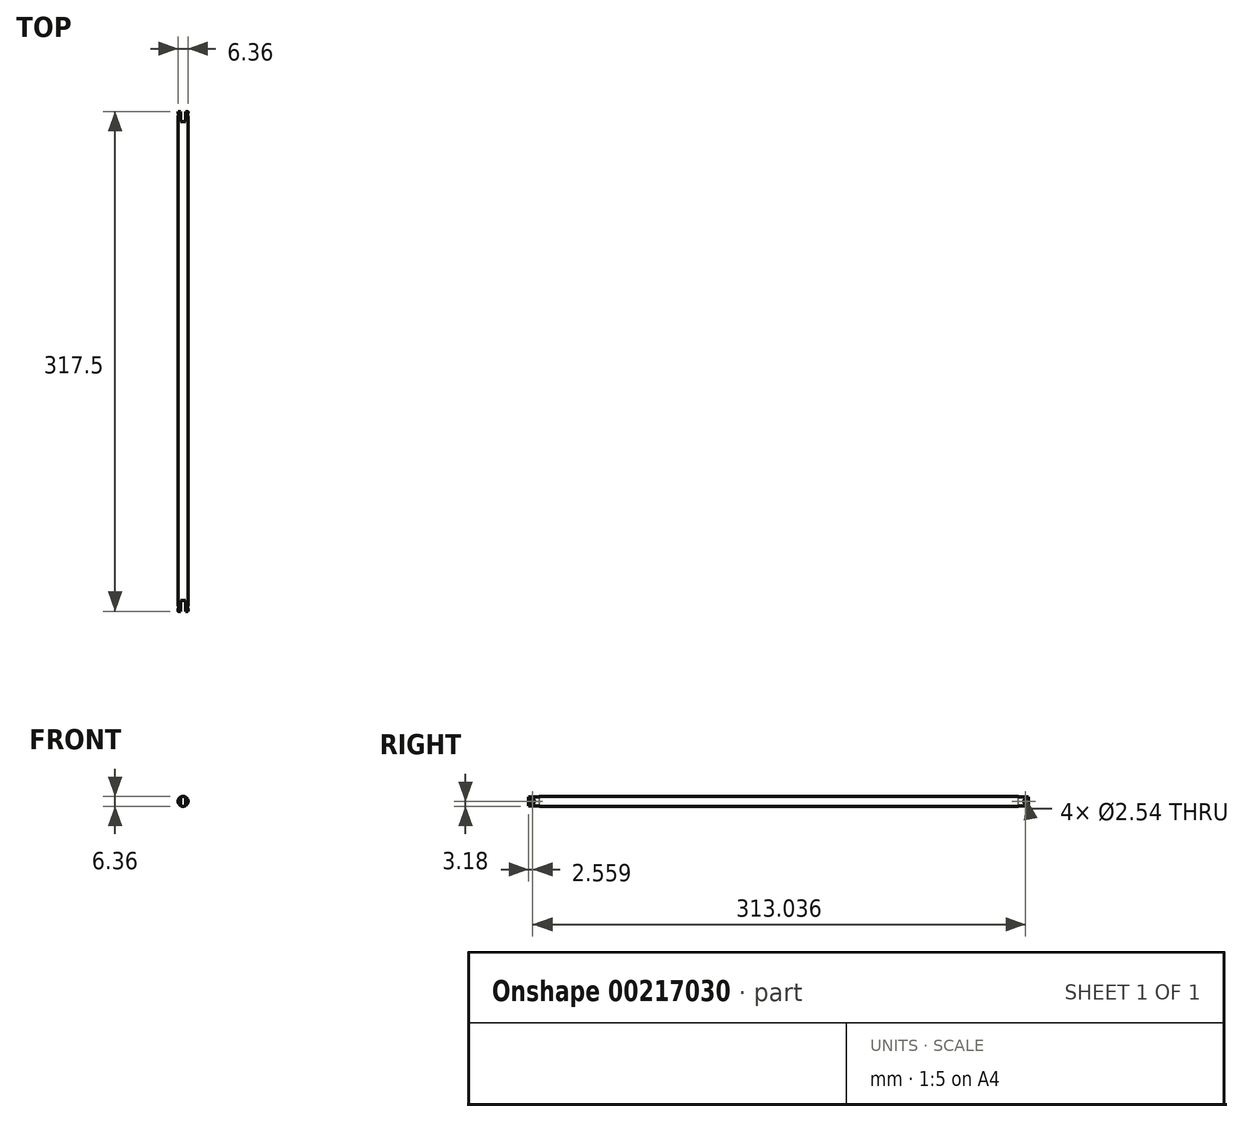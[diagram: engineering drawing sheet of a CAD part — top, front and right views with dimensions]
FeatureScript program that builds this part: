
annotation { "Feature Type Name" : "Feature", "Feature Type Description" : "" }
export const myFeature = defineFeature(function(context is Context, id is Id, definition is map)
    precondition{}
    {
        {
            var Q0;
            Q0=qCreatedBy(makeId("Front.planeOp"),FACE);
            var sketch = newSketch(context, id + "F0", { "sketchPlane" : qUnion([Q0])});
            skCircle(sketch, "E0", {"center": v(0, 0) * mm, "radius": 3.18 * mm});
            skSolve(sketch);
        }
        {
            var Q0;
            Q0=makeQuery(id+"F0.imprint","IMPRINT",FACE,{"disambiguationData":[TD([[makeQuery(id+"F0.imprint","IMPRINT",EDGE,{"derivedFrom":sQuery(id+"F0.wireOp",EDGE,"E0")}),1.0]])]});
            extrude(context, id + "F1", {"entities" : qUnion([Q0]), "depth" : 298.45 * mm});
        }
        {
            var Q0;
            Q0=qCreatedBy(makeId("Top.planeOp"),FACE);
            var sketch = newSketch(context, id + "F2", { "sketchPlane" : qUnion([Q0])});
            skLineSegment(sketch, "E1.bottom", {"start": v(1.59, -6.54) * mm, "end": v(-1.59, -6.54) * mm});
            skLineSegment(sketch, "E1.top", {"start": v(1.59, 6.54) * mm, "end": v(-1.59, 6.54) * mm});
            skLineSegment(sketch, "E1.left", {"start": v(1.59, -6.54) * mm, "end": v(1.59, 6.54) * mm});
            skLineSegment(sketch, "E1.right", {"start": v(-1.59, -6.54) * mm, "end": v(-1.59, 6.54) * mm});
            skPoint(sketch, "E1.middle", {"position": v(0, 0) * mm});
            skSolve(sketch);
        }
        {
            var Q0;
            Q0 = qSketchRegion(id + "F2", true);
            extrude(context, id + "F3", {"entities" : qUnion([Q0]), "operationType" : NewBodyOperationType.REMOVE, "oppositeDirection" : true, "depth" : 25.4 * mm, "symmetric" : true});
        }
        {
            var Q0;
            Q0=qCreatedBy(makeId("Right.planeOp"),FACE);
            var sketch = newSketch(context, id + "F4", { "sketchPlane" : qUnion([Q0])});
            skLineSegment(sketch, "E2", {"start": v(0, 0) * mm, "end": v(-1.9, 0) * mm, "construction": true});
            skCircle(sketch, "E3", {"center": v(-1.9, 0) * mm, "radius": 1.27 * mm});
            skSolve(sketch);
        }
        {
            var Q0;
            Q0 = qSketchRegion(id + "F4", true);
            extrude(context, id + "F5", {"entities" : qUnion([Q0]), "operationType" : NewBodyOperationType.REMOVE, "oppositeDirection" : true, "depth" : 25.4 * mm, "symmetric" : true});
        }
        {
            var Q0;
            Q0=makeQuery(id+"F1.opExtrude","CAP_FACE",FACE,{"disambiguationData":[OSD([sQuery(id+"F0.wireOp",EDGE,"E0")])],"isStart":false});
            extrude(context, id + "F6", {"entities" : qUnion([Q0]), "operationType" : NewBodyOperationType.ADD, "depth" : 19.05 * mm});
        }
        {
            var Q0;
            Q0=qCreatedBy(makeId("Top.planeOp"),FACE);
            var sketch = newSketch(context, id + "F7", { "sketchPlane" : qUnion([Q0])});
            skLineSegment(sketch, "E4.bottom", {"start": v(1.59, -323.33) * mm, "end": v(-1.59, -323.33) * mm});
            skLineSegment(sketch, "E4.top", {"start": v(1.59, -310.63) * mm, "end": v(-1.59, -310.63) * mm});
            skLineSegment(sketch, "E4.left", {"start": v(1.59, -323.33) * mm, "end": v(1.59, -310.63) * mm});
            skLineSegment(sketch, "E4.right", {"start": v(-1.59, -323.33) * mm, "end": v(-1.59, -310.63) * mm});
            skPoint(sketch, "E4.middle", {"position": v(0, -316.98) * mm});
            skSolve(sketch);
        }
        {
            var Q0;
            Q0=makeQuery(id+"F7.imprint","IMPRINT",FACE,{"disambiguationData":[TD([[makeQuery(id+"F7.imprint","IMPRINT",EDGE,{"derivedFrom":sQuery(id+"F7.wireOp",EDGE,"E4.bottom")}),-1.0]])]});
            extrude(context, id + "F8", {"entities" : qUnion([Q0]), "operationType" : NewBodyOperationType.REMOVE, "oppositeDirection" : true, "depth" : 25.4 * mm, "symmetric" : true});
        }
        {
            var Q0;
            Q0=qCreatedBy(makeId("Right.planeOp"),FACE);
            var sketch = newSketch(context, id + "F9", { "sketchPlane" : qUnion([Q0])});
            skCircle(sketch, "E5", {"center": v(-314.94, 0) * mm, "radius": 1.27 * mm});
            skSolve(sketch);
        }
        {
            var Q0;
            Q0=makeQuery(id+"F9.imprint","IMPRINT",FACE,{"disambiguationData":[TD([[makeQuery(id+"F9.imprint","IMPRINT",EDGE,{"derivedFrom":sQuery(id+"F9.wireOp",EDGE,"E5")}),1.0]])]});
            extrude(context, id + "F10", {"entities" : qUnion([Q0]), "operationType" : NewBodyOperationType.REMOVE, "oppositeDirection" : true, "depth" : 25.4 * mm, "symmetric" : true});
        }
    });
